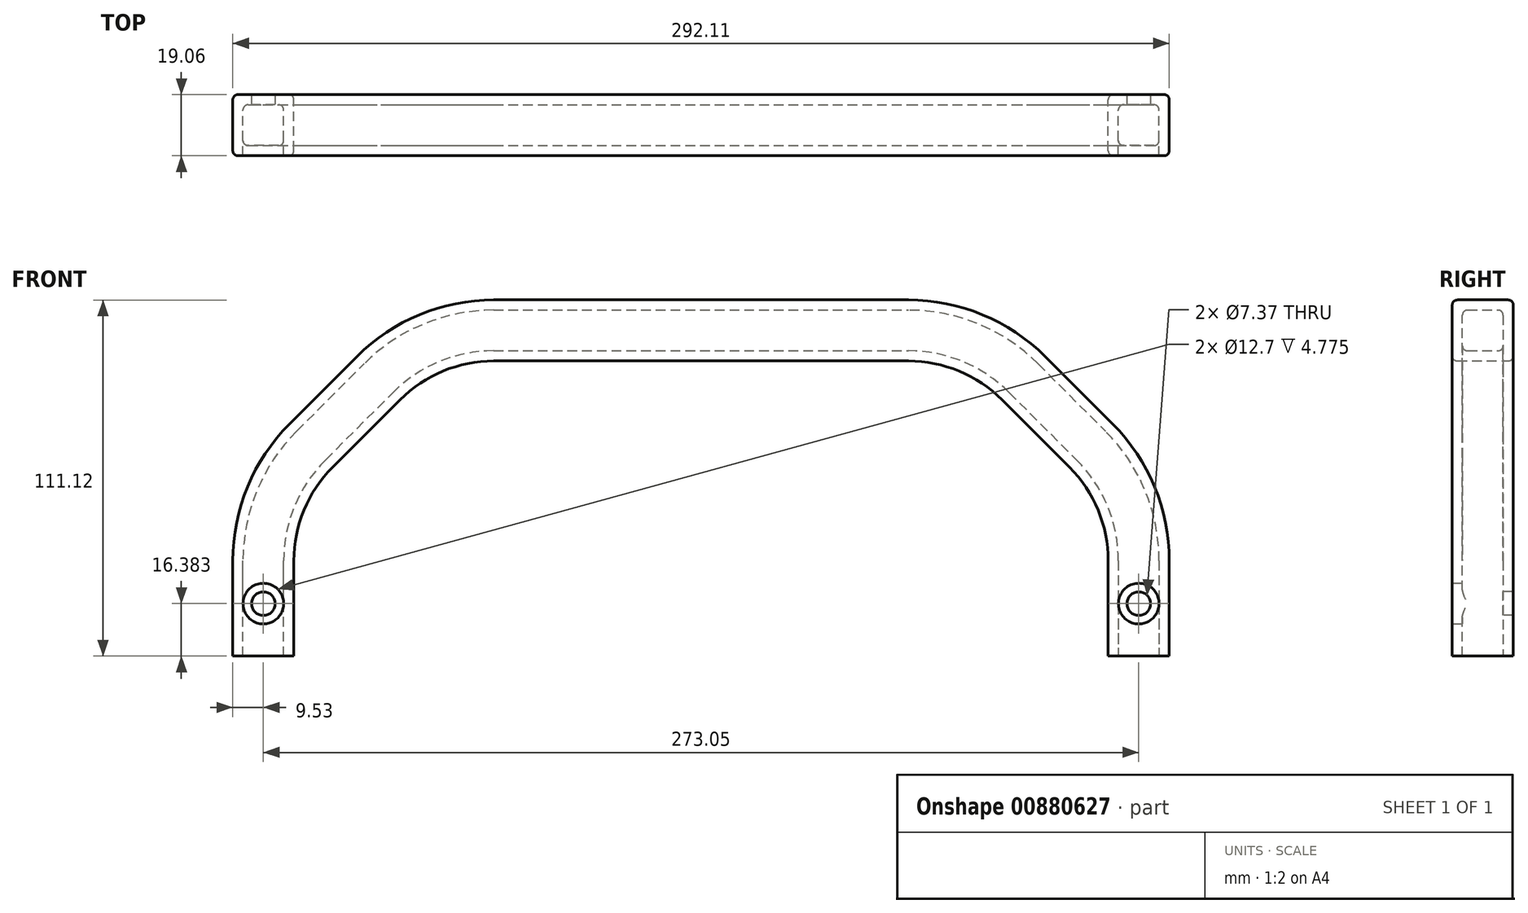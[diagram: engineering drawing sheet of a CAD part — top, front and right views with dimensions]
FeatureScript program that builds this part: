
annotation { "Feature Type Name" : "Feature", "Feature Type Description" : "" }
export const myFeature = defineFeature(function(context is Context, id is Id, definition is map)
    precondition{}
    {
        {
            var Q0;
            Q0=qCreatedBy(makeId("Front.planeOp"),FACE);
            var sketch = newSketch(context, id + "F0", { "sketchPlane" : qUnion([Q0])});
            skLineSegment(sketch, "E0", {"start": v(0, 0) * mm, "end": v(0, 29.76) * mm});
            skLineSegment(sketch, "E1", {"start": v(14.88, 65.68) * mm, "end": v(35.92, 86.72) * mm});
            skLineSegment(sketch, "E2", {"start": v(71.84, 101.6) * mm, "end": v(201.2, 101.6) * mm});
            skLineSegment(sketch, "E3", {"start": v(237.13, 86.72) * mm, "end": v(258.17, 65.68) * mm});
            skLineSegment(sketch, "E4", {"start": v(273.05, 29.76) * mm, "end": v(273.05, 0) * mm});
            skPoint(sketch, "E5.visualSharp", {"position": v(273.05, 50.8) * mm});
            skArc(sketch, "E5.filletArc", {"start": v(273.05, 29.76) * mm, "mid": v(269.18, 49.2) * mm, "end": v(258.17, 65.68) * mm});
            skPoint(sketch, "E6.visualSharp", {"position": v(222.25, 101.6) * mm});
            skArc(sketch, "E6.filletArc", {"start": v(237.13, 86.72) * mm, "mid": v(220.65, 97.73) * mm, "end": v(201.2, 101.6) * mm});
            skPoint(sketch, "E7.visualSharp", {"position": v(50.8, 101.6) * mm});
            skArc(sketch, "E7.filletArc", {"start": v(71.84, 101.6) * mm, "mid": v(52.4, 97.73) * mm, "end": v(35.92, 86.72) * mm});
            skPoint(sketch, "E8.visualSharp", {"position": v(0, 50.8) * mm});
            skArc(sketch, "E8.filletArc", {"start": v(14.88, 65.68) * mm, "mid": v(3.87, 49.2) * mm, "end": v(0, 29.76) * mm});
            skSolve(sketch);
        }
        {
            var Q0;
            Q0=qCreatedBy(makeId("Top.planeOp"),FACE);
            var sketch = newSketch(context, id + "F1", { "sketchPlane" : qUnion([Q0])});
            skLineSegment(sketch, "E9.bottom", {"start": v(-7.92, -9.53) * mm, "end": v(7.92, -9.53) * mm});
            skLineSegment(sketch, "E9.top", {"start": v(-7.92, 9.53) * mm, "end": v(7.92, 9.53) * mm});
            skLineSegment(sketch, "E9.left", {"start": v(-9.53, -7.92) * mm, "end": v(-9.53, 7.92) * mm});
            skLineSegment(sketch, "E9.right", {"start": v(9.53, -7.92) * mm, "end": v(9.53, 7.92) * mm});
            skLineSegment(sketch, "E10", {"start": v(0, -9.53) * mm, "end": v(0, 9.53) * mm, "construction": true});
            skLineSegment(sketch, "E11.0", {"start": v(-4.75, 6.35) * mm, "end": v(4.75, 6.35) * mm});
            skLineSegment(sketch, "E11.1", {"start": v(6.35, -4.75) * mm, "end": v(6.35, 4.75) * mm});
            skLineSegment(sketch, "E11.2", {"start": v(-4.75, -6.35) * mm, "end": v(4.75, -6.35) * mm});
            skLineSegment(sketch, "E11.3", {"start": v(-6.35, -4.75) * mm, "end": v(-6.35, 4.75) * mm});
            skPoint(sketch, "E12.visualSharp", {"position": v(9.53, -9.53) * mm});
            skArc(sketch, "E12.filletArc", {"start": v(7.92, -9.53) * mm, "mid": v(9.06, -9.06) * mm, "end": v(9.53, -7.92) * mm});
            skPoint(sketch, "E13.visualSharp", {"position": v(9.53, 9.53) * mm});
            skArc(sketch, "E13.filletArc", {"start": v(9.53, 7.92) * mm, "mid": v(9.06, 9.06) * mm, "end": v(7.92, 9.53) * mm});
            skPoint(sketch, "E14.visualSharp", {"position": v(-9.53, 9.53) * mm});
            skArc(sketch, "E14.filletArc", {"start": v(-7.92, 9.53) * mm, "mid": v(-9.06, 9.06) * mm, "end": v(-9.53, 7.92) * mm});
            skPoint(sketch, "E15.visualSharp", {"position": v(-9.53, -9.53) * mm});
            skArc(sketch, "E15.filletArc", {"start": v(-9.53, -7.92) * mm, "mid": v(-9.06, -9.06) * mm, "end": v(-7.92, -9.53) * mm});
            skPoint(sketch, "E16.visualSharp", {"position": v(6.35, -6.35) * mm});
            skArc(sketch, "E16.filletArc", {"start": v(4.75, -6.35) * mm, "mid": v(5.88, -5.88) * mm, "end": v(6.35, -4.75) * mm});
            skPoint(sketch, "E17.visualSharp", {"position": v(-6.35, 6.35) * mm});
            skArc(sketch, "E17.filletArc", {"start": v(-4.75, 6.35) * mm, "mid": v(-5.88, 5.88) * mm, "end": v(-6.35, 4.75) * mm});
            skPoint(sketch, "E18.visualSharp", {"position": v(-6.35, -6.35) * mm});
            skArc(sketch, "E18.filletArc", {"start": v(-6.35, -4.75) * mm, "mid": v(-5.88, -5.88) * mm, "end": v(-4.75, -6.35) * mm});
            skPoint(sketch, "E19.visualSharp", {"position": v(6.35, 6.35) * mm});
            skArc(sketch, "E19.filletArc", {"start": v(6.35, 4.75) * mm, "mid": v(5.88, 5.88) * mm, "end": v(4.75, 6.35) * mm});
            skSolve(sketch);
        }
        {
            var Q0;
            Q0 = qSketchRegion(id + "F1", true);
            var Q1;
            Q1 = qConstructionFilter(qBodyType(qCreatedBy(id + "F0" ,EDGE), BodyType.WIRE), ConstructionObject.NO);
            sweep(context, id + "F2", {"profiles" : qUnion([Q0]), "path" : qUnion([Q1])});
        }
        {
            var Q0;
            Q0=qCreatedBy(makeId("Front.planeOp"),FACE);
            var sketch = newSketch(context, id + "F3", { "sketchPlane" : qUnion([Q0])});
            skCircle(sketch, "E20", {"center": v(0, 16.38) * mm, "radius": 3.68 * mm});
            skCircle(sketch, "E21", {"center": v(273.05, 16.38) * mm, "radius": 3.68 * mm});
            skSolve(sketch);
        }
        {
            var Q0;
            Q0 = qSketchRegion(id + "F3", true);
            extrude(context, id + "F4", {"entities" : qUnion([Q0]), "operationType" : NewBodyOperationType.REMOVE, "oppositeDirection" : true, "depth" : 25.4 * mm, "offsetDistance" : 25.4 * mm});
        }
        {
            var Q0;
            Q0=qCreatedBy(makeId("Front.planeOp"),FACE);
            var sketch = newSketch(context, id + "F5", { "sketchPlane" : qUnion([Q0])});
            skCircle(sketch, "E22", {"center": v(273.05, 16.38) * mm, "radius": 6.35 * mm});
            skCircle(sketch, "E23", {"center": v(0, 16.38) * mm, "radius": 6.35 * mm});
            skSolve(sketch);
        }
        {
            var Q0;
            Q0 = qSketchRegion(id + "F5", true);
            extrude(context, id + "F6", {"entities" : qUnion([Q0]), "operationType" : NewBodyOperationType.REMOVE, "depth" : 25.4 * mm, "offsetDistance" : 25.4 * mm});
        }
    });
